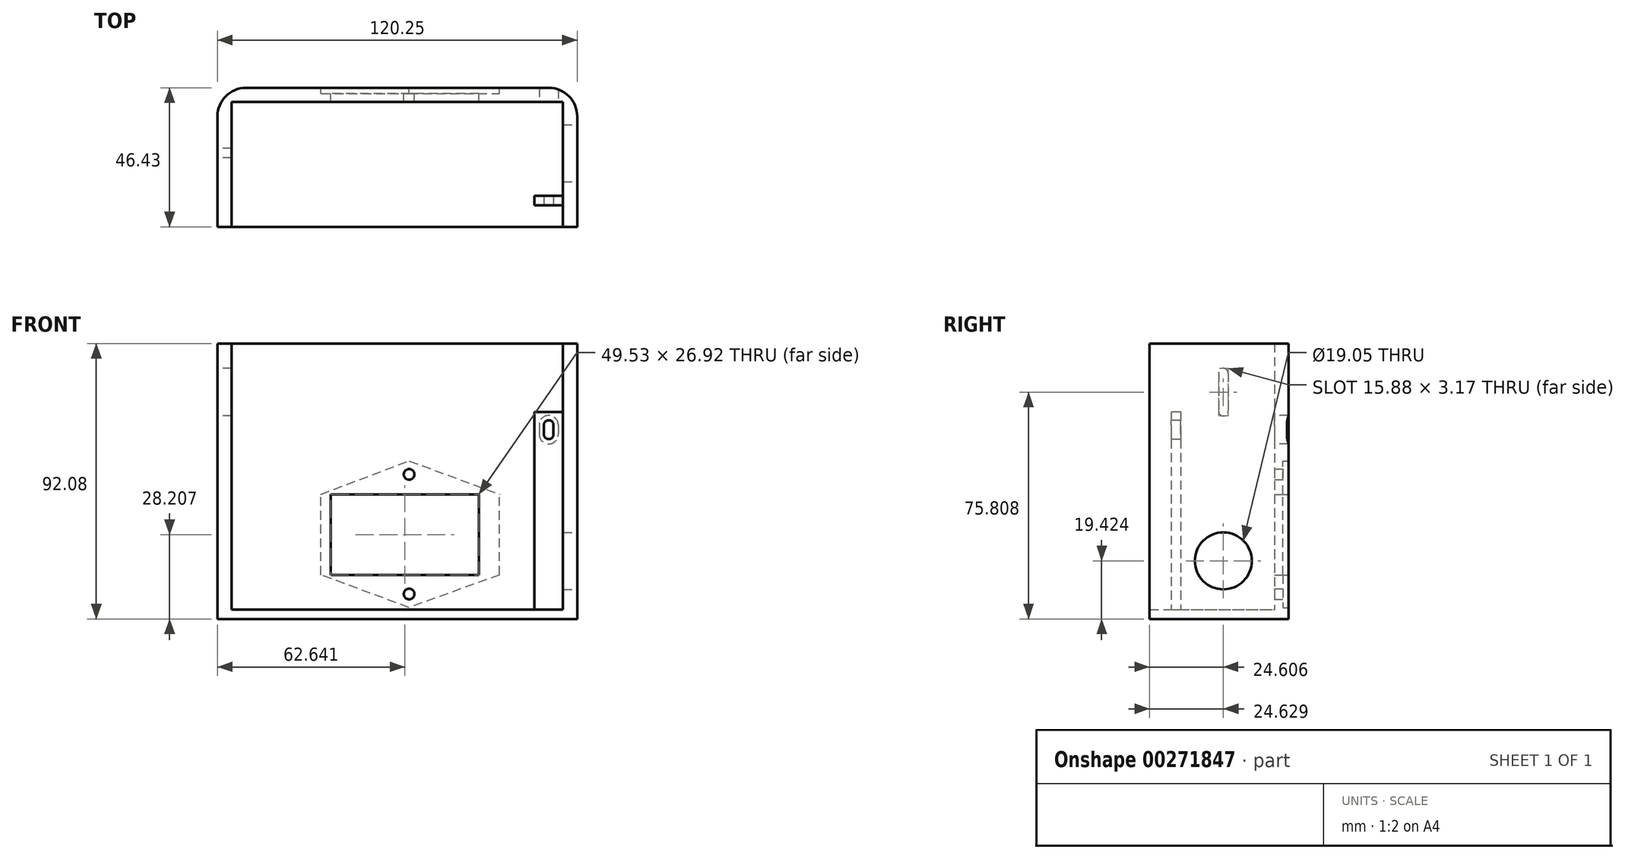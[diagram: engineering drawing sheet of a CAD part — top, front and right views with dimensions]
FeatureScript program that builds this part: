
annotation { "Feature Type Name" : "Feature", "Feature Type Description" : "" }
export const myFeature = defineFeature(function(context is Context, id is Id, definition is map)
    precondition{}
    {
        {
            var Q0;
            Q0=qCreatedBy(makeId("Top.planeOp"),FACE);
            var sketch = newSketch(context, id + "F0", { "sketchPlane" : qUnion([Q0])});
            skLineSegment(sketch, "E0.bottom", {"start": v(0, 0) * mm, "end": v(120.25, 0) * mm});
            skLineSegment(sketch, "E0.top", {"start": v(0, 46.43) * mm, "end": v(120.25, 46.43) * mm});
            skLineSegment(sketch, "E0.left", {"start": v(0, 0) * mm, "end": v(0, 46.43) * mm});
            skLineSegment(sketch, "E0.right", {"start": v(120.25, 0) * mm, "end": v(120.25, 46.43) * mm});
            skLineSegment(sketch, "E1.0", {"start": v(115.5, 0) * mm, "end": v(115.5, 41.67) * mm});
            skLineSegment(sketch, "E1.1", {"start": v(4.76, 41.67) * mm, "end": v(115.5, 41.67) * mm});
            skLineSegment(sketch, "E1.2", {"start": v(4.76, 0) * mm, "end": v(4.76, 41.67) * mm});
            skSolve(sketch);
        }
        {
            var Q0;
            Q0=makeQuery(id+"F0.imprint","IMPRINT",FACE,{"disambiguationData":[TD([[makeQuery(id+"F0.imprint","IMPRINT",EDGE,{"derivedFrom":sQuery(id+"F0.wireOp",EDGE,"E0.top")}),-1.0]])]});
            extrude(context, id + "F1", {"entities" : qUnion([Q0]), "depth" : 88.9 * mm});
        }
        {
            var Q0;
            Q0 = qSketchRegion(id + "F0", true);
            extrude(context, id + "F2", {"entities" : qUnion([Q0]), "operationType" : NewBodyOperationType.ADD, "oppositeDirection" : true, "depth" : 3.17 * mm});
        }
        {
            var Q0;
            Q0=makeQuery(id+"F2.opExtrude","CAP_FACE",FACE,{"disambiguationData":[OSD([sQuery(id+"F0.wireOp",EDGE,"E0.bottom"),sQuery(id+"F0.wireOp",EDGE,"E0.top"),sQuery(id+"F0.wireOp",EDGE,"E0.left"),sQuery(id+"F0.wireOp",EDGE,"E0.right")])],"isStart":true});
            var sketch = newSketch(context, id + "F3", { "sketchPlane" : qUnion([Q0])});
            skLineSegment(sketch, "E2.bottom", {"start": v(115.5, 7.14) * mm, "end": v(105.97, 7.14) * mm});
            skLineSegment(sketch, "E2.top", {"start": v(115.5, 10.32) * mm, "end": v(105.97, 10.32) * mm});
            skLineSegment(sketch, "E2.left", {"start": v(115.5, 7.14) * mm, "end": v(115.5, 10.32) * mm});
            skLineSegment(sketch, "E2.right", {"start": v(105.97, 7.14) * mm, "end": v(105.97, 10.32) * mm});
            skSolve(sketch);
        }
        {
            var Q0;
            Q0 = qSketchRegion(id + "F3", true);
            var Q1;
            Q1=makeQuery(id+"F1.opExtrude","CAP_FACE",FACE,{"disambiguationData":[OSD([sQuery(id+"F0.wireOp",EDGE,"E0.bottom"),sQuery(id+"F0.wireOp",EDGE,"E0.top"),sQuery(id+"F0.wireOp",EDGE,"E0.left"),sQuery(id+"F0.wireOp",EDGE,"E0.right"),sQuery(id+"F0.wireOp",EDGE,"E1.0"),sQuery(id+"F0.wireOp",EDGE,"E1.1"),sQuery(id+"F0.wireOp",EDGE,"E1.2")])],"isStart":false});
            extrude(context, id + "F4", {"entities" : qUnion([Q0]), "operationType" : NewBodyOperationType.ADD, "endBound" : BoundingType.UP_TO_SURFACE, "endBoundEntityFace" : qUnion([Q1]), "depth" : (1 + (61 / 64)) * mm});
        }
        {
            var Q0;
            Q0=makeQuery(id+"F4.opExtrude","SWEPT_FACE",FACE,{"disambiguationData":[OSD([sQuery(id+"F3.wireOp",EDGE,"E2.bottom")])]});
            var sketch = newSketch(context, id + "F5", { "sketchPlane" : qUnion([Q0])});
            skLineSegment(sketch, "E3.bottom", {"start": v(105.97, 88.9) * mm, "end": v(115.5, 88.9) * mm});
            skLineSegment(sketch, "E3.top", {"start": v(105.97, 66.04) * mm, "end": v(115.5, 66.04) * mm});
            skLineSegment(sketch, "E3.left", {"start": v(105.97, 88.9) * mm, "end": v(105.97, 66.04) * mm});
            skLineSegment(sketch, "E3.right", {"start": v(115.5, 88.9) * mm, "end": v(115.5, 66.04) * mm});
            skArc(sketch, "E4", {"start": v(112.32, 61.67) * mm, "mid": v(110.73, 63.26) * mm, "end": v(109.14, 61.67) * mm});
            skLineSegment(sketch, "E5.0", {"start": v(105.97, 63.26) * mm, "end": v(115.5, 63.26) * mm, "construction": true});
            skLineSegment(sketch, "E6", {"start": v(109.14, 61.67) * mm, "end": v(109.14, 58.5) * mm});
            skArc(sketch, "E7.0.1.0", {"start": v(109.14, 58.5) * mm, "mid": v(110.73, 56.91) * mm, "end": v(112.32, 58.5) * mm});
            skLineSegment(sketch, "E7.direction2", {"start": v(110.73, 61.67) * mm, "end": v(110.73, 58.5) * mm, "construction": true});
            skLineSegment(sketch, "E8", {"start": v(112.32, 61.67) * mm, "end": v(112.32, 58.5) * mm});
            skSolve(sketch);
        }
        {
            var Q0;
            Q0=makeQuery(id+"F5.imprint","IMPRINT",FACE,{"disambiguationData":[TD([[makeQuery(id+"F5.imprint","IMPRINT",EDGE,{"derivedFrom":sQuery(id+"F5.wireOp",EDGE,"E3.bottom")}),1.0]])]});
            var Q1;
            Q1=makeQuery(id+"F5.imprint","IMPRINT",FACE,{"disambiguationData":[TD([[makeQuery(id+"F5.imprint","IMPRINT",EDGE,{"derivedFrom":sQuery(id+"F5.wireOp",EDGE,"E4")}),1.0]])]});
            extrude(context, id + "F6", {"entities" : qUnion([Q0, Q1]), "operationType" : NewBodyOperationType.REMOVE, "endBound" : BoundingType.UP_TO_NEXT, "oppositeDirection" : true, "depth" : 25.4 * mm});
        }
        {
            var Q0;
            {var subQ0=sQuery(id+"F0.wireOp",EDGE,"E0.left");Q0=makeQuery(id+"F2.boolean.opBoolean","MERGE",FACE,{"derivedFrom":[makeQuery(id+"F1.opExtrude","SWEPT_FACE",FACE,{"disambiguationData":[OSD([subQ0])]}),makeQuery(id+"F2.opExtrude","SWEPT_FACE",FACE,{"disambiguationData":[OSD([subQ0])]})]});}
            var sketch = newSketch(context, id + "F7", { "sketchPlane" : qUnion([Q0])});
            skArc(sketch, "E9", {"start": v(-23.02, 78.98) * mm, "mid": v(-24.6, 80.57) * mm, "end": v(-26.2, 78.98) * mm});
            skLineSegment(sketch, "E10", {"start": v(-26.2, 78.98) * mm, "end": v(-26.2, 66.28) * mm});
            skArc(sketch, "E11.0.1.0", {"start": v(-26.2, 66.28) * mm, "mid": v(-24.6, 64.7) * mm, "end": v(-23.02, 66.28) * mm});
            skLineSegment(sketch, "E11.direction1", {"start": v(-24.6, 78.98) * mm, "end": v(0.8, 78.98) * mm, "construction": true});
            skLineSegment(sketch, "E11.direction2", {"start": v(-24.6, 78.98) * mm, "end": v(-24.6, 66.28) * mm, "construction": true});
            skLineSegment(sketch, "E12", {"start": v(-23.02, 78.98) * mm, "end": v(-23.02, 66.28) * mm});
            skSolve(sketch);
        }
        {
            var Q0;
            Q0=makeQuery(id+"F7.imprint","IMPRINT",FACE,{"disambiguationData":[TD([[makeQuery(id+"F7.imprint","IMPRINT",EDGE,{"derivedFrom":sQuery(id+"F7.wireOp",EDGE,"E9")}),1.0]])]});
            extrude(context, id + "F8", {"entities" : qUnion([Q0]), "operationType" : NewBodyOperationType.REMOVE, "endBound" : BoundingType.UP_TO_NEXT, "oppositeDirection" : true, "depth" : 25.4 * mm});
        }
        {
            var Q0;
            {var subQ0=sQuery(id+"F0.wireOp",EDGE,"E0.right");var subQ1=sQuery(id+"F0.wireOp",EDGE,"E0.top");Q0=makeQuery(id+"F2.boolean.opBoolean","MERGE",EDGE,{"derivedFrom":[makeQuery(id+"F1.opExtrude","SWEPT_EDGE",EDGE,{"disambiguationData":[OSD([subQ1,subQ0])]}),makeQuery(id+"F2.opExtrude","SWEPT_EDGE",EDGE,{"disambiguationData":[OSD([subQ1,subQ0])]})]});}
            var Q1;
            {var subQ0=sQuery(id+"F0.wireOp",EDGE,"E0.left");var subQ1=sQuery(id+"F0.wireOp",EDGE,"E0.top");Q1=makeQuery(id+"F2.boolean.opBoolean","MERGE",EDGE,{"derivedFrom":[makeQuery(id+"F1.opExtrude","SWEPT_EDGE",EDGE,{"disambiguationData":[OSD([subQ1,subQ0])]}),makeQuery(id+"F2.opExtrude","SWEPT_EDGE",EDGE,{"disambiguationData":[OSD([subQ1,subQ0])]})]});}
            fillet(context, id + "F9", {"entities" : qUnion([Q0, Q1]), "radius" : 9.52 * mm, "tangentPropagation" : true, "allowEdgeOverflow" : false});
        }
        {
            var Q0;
            {var subQ0=sQuery(id+"F0.wireOp",EDGE,"E0.top");Q0=makeQuery(id+"F2.boolean.opBoolean","MERGE",FACE,{"derivedFrom":[makeQuery(id+"F1.opExtrude","SWEPT_FACE",FACE,{"disambiguationData":[OSD([subQ0])]}),makeQuery(id+"F2.opExtrude","SWEPT_FACE",FACE,{"disambiguationData":[OSD([subQ0])]})]});}
            var sketch = newSketch(context, id + "F10", { "sketchPlane" : qUnion([Q0])});
            skLineSegment(sketch, "E13.bottom", {"start": v(-87.4, 11.57) * mm, "end": v(-37.88, 11.57) * mm});
            skLineSegment(sketch, "E13.top", {"start": v(-87.4, 38.49) * mm, "end": v(-37.88, 38.49) * mm});
            skLineSegment(sketch, "E13.left", {"start": v(-87.4, 11.57) * mm, "end": v(-87.4, 38.49) * mm});
            skLineSegment(sketch, "E13.right", {"start": v(-37.88, 11.57) * mm, "end": v(-37.88, 38.49) * mm});
            skLineSegment(sketch, "E14", {"start": v(-94.31, 11.57) * mm, "end": v(-94.31, 38.49) * mm});
            skLineSegment(sketch, "E15", {"start": v(-34.62, 11.57) * mm, "end": v(-34.62, 38.49) * mm});
            skLineSegment(sketch, "E16", {"start": v(-94.31, 38.49) * mm, "end": v(-34.62, 38.49) * mm, "construction": true});
            skLineSegment(sketch, "E17", {"start": v(-37.88, 11.57) * mm, "end": v(-34.62, 11.57) * mm, "construction": true});
            skLineSegment(sketch, "E18", {"start": v(-34.62, 38.49) * mm, "end": v(-64.09, 49.67) * mm});
            skLineSegment(sketch, "E19", {"start": v(-64.09, 49.67) * mm, "end": v(-64.09, 0.64) * mm, "construction": true});
            skLineSegment(sketch, "E20", {"start": v(-64.09, 49.67) * mm, "end": v(-94.31, 38.49) * mm});
            skLineSegment(sketch, "E21", {"start": v(-94.31, 11.57) * mm, "end": v(-64.09, 0.64) * mm});
            skLineSegment(sketch, "E22", {"start": v(-64.09, 0.64) * mm, "end": v(-34.62, 11.57) * mm});
            skCircle(sketch, "E23", {"center": v(-64.09, 45.14) * mm, "radius": 1.78 * mm});
            skCircle(sketch, "E24", {"center": v(-64.09, 5.16) * mm, "radius": 1.78 * mm});
            skSolve(sketch);
        }
        {
            var Q0;
            Q0=makeQuery(id+"F10.imprint","IMPRINT",FACE,{"disambiguationData":[TD([[makeQuery(id+"F10.imprint","IMPRINT",EDGE,{"derivedFrom":sQuery(id+"F10.wireOp",EDGE,"E13.bottom")}),1.0]])]});
            var Q1;
            Q1=makeQuery(id+"F10.imprint","IMPRINT",FACE,{"disambiguationData":[TD([[makeQuery(id+"F10.imprint","IMPRINT",EDGE,{"derivedFrom":sQuery(id+"F10.wireOp",EDGE,"E23")}),1.0]])]});
            var Q2;
            Q2=makeQuery(id+"F10.imprint","IMPRINT",FACE,{"disambiguationData":[TD([[makeQuery(id+"F10.imprint","IMPRINT",EDGE,{"derivedFrom":sQuery(id+"F10.wireOp",EDGE,"E24")}),1.0]])]});
            extrude(context, id + "F11", {"entities" : qUnion([Q0, Q1, Q2]), "operationType" : NewBodyOperationType.REMOVE, "endBound" : BoundingType.UP_TO_NEXT, "oppositeDirection" : true, "depth" : 25.4 * mm});
        }
        {
            var Q0;
            Q0=makeQuery(id+"F10.imprint","IMPRINT",FACE,{"disambiguationData":[TD([[makeQuery(id+"F10.imprint","IMPRINT",EDGE,{"derivedFrom":sQuery(id+"F10.wireOp",EDGE,"E13.bottom")}),-1.0]])]});
            extrude(context, id + "F12", {"entities" : qUnion([Q0]), "operationType" : NewBodyOperationType.REMOVE, "oppositeDirection" : true, "depth" : 1.9 * mm});
        }
        {
            var Q0;
            Q0=makeQuery(id+"F1.opExtrude","SWEPT_FACE",FACE,{"disambiguationData":[OSD([sQuery(id+"F0.wireOp",EDGE,"E1.1")])]});
            var sketch = newSketch(context, id + "F13", { "sketchPlane" : qUnion([Q0])});
            skArc(sketch, "E25.0", {"start": v(112.32, 61.67) * mm, "mid": v(110.73, 63.26) * mm, "end": v(109.14, 61.67) * mm, "construction": true});
            skArc(sketch, "E26", {"start": v(113.9, 61.67) * mm, "mid": v(110.73, 64.85) * mm, "end": v(107.55, 61.67) * mm});
            skArc(sketch, "E27.0", {"start": v(112.32, 58.5) * mm, "mid": v(110.73, 56.91) * mm, "end": v(109.14, 58.5) * mm, "construction": true});
            skArc(sketch, "E28", {"start": v(107.55, 58.5) * mm, "mid": v(110.73, 55.32) * mm, "end": v(113.9, 58.5) * mm});
            skLineSegment(sketch, "E29", {"start": v(107.55, 61.67) * mm, "end": v(107.55, 58.5) * mm});
            skLineSegment(sketch, "E30", {"start": v(113.9, 61.67) * mm, "end": v(113.9, 58.5) * mm});
            skSolve(sketch);
        }
        {
            var Q0;
            Q0 = qSketchRegion(id + "F13", true);
            extrude(context, id + "F14", {"entities" : qUnion([Q0]), "operationType" : NewBodyOperationType.REMOVE, "endBound" : BoundingType.UP_TO_NEXT, "oppositeDirection" : true, "depth" : 25.4 * mm});
        }
        {
            var Q0;
            {var subQ0=sQuery(id+"F0.wireOp",EDGE,"E0.right");Q0=makeQuery(id+"F2.boolean.opBoolean","MERGE",FACE,{"derivedFrom":[makeQuery(id+"F1.opExtrude","SWEPT_FACE",FACE,{"disambiguationData":[OSD([subQ0])]}),makeQuery(id+"F2.opExtrude","SWEPT_FACE",FACE,{"disambiguationData":[OSD([subQ0])]})]});}
            var sketch = newSketch(context, id + "F15", { "sketchPlane" : qUnion([Q0])});
            skCircle(sketch, "E31", {"center": v(24.63, 16.24) * mm, "radius": 9.53 * mm});
            skSolve(sketch);
        }
        {
            var Q0;
            Q0 = qSketchRegion(id + "F15", true);
            extrude(context, id + "F16", {"entities" : qUnion([Q0]), "operationType" : NewBodyOperationType.REMOVE, "endBound" : BoundingType.UP_TO_NEXT, "oppositeDirection" : true, "depth" : 25.4 * mm});
        }
    });
